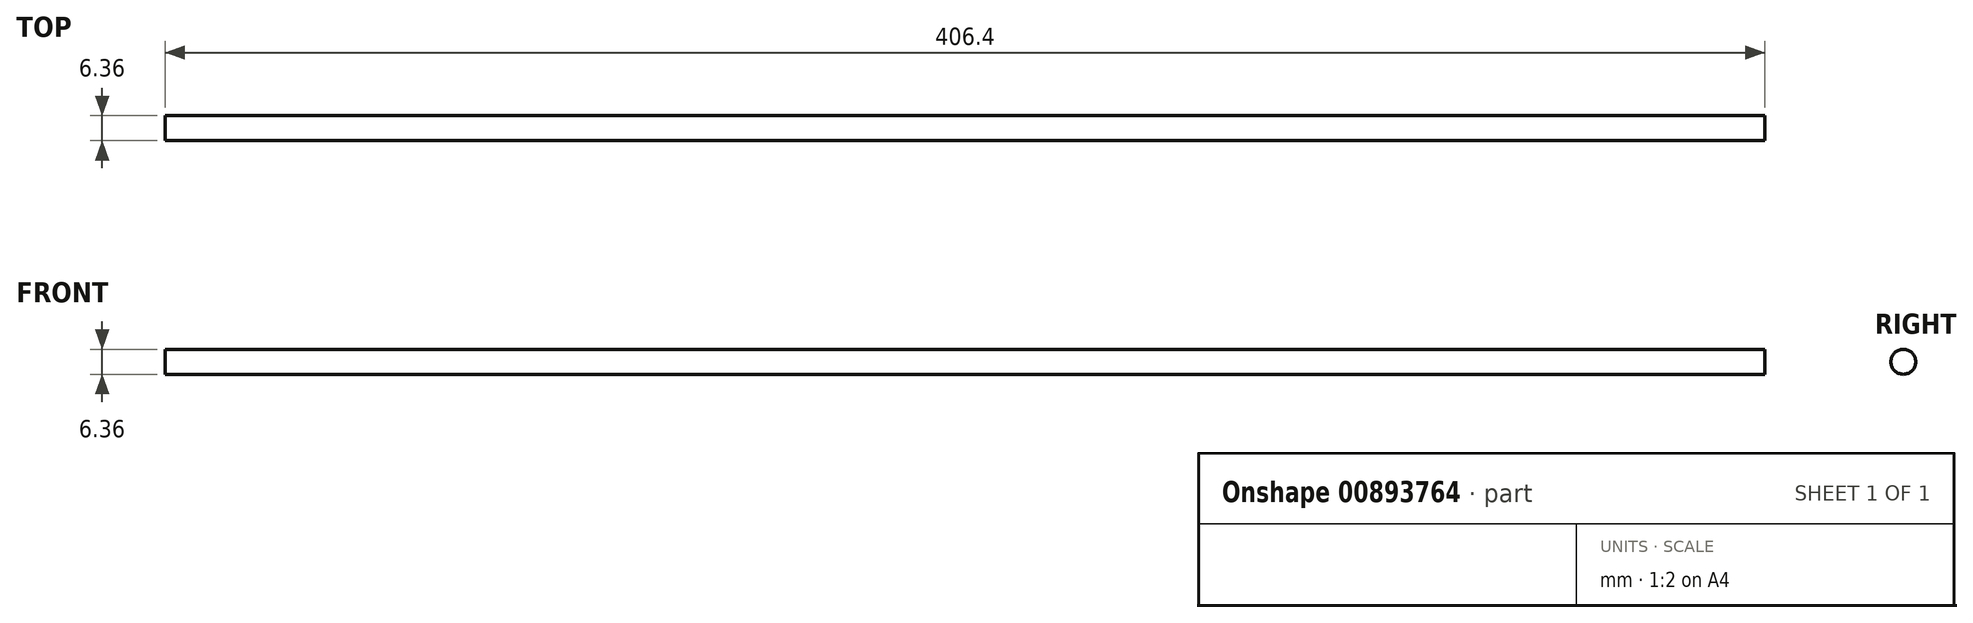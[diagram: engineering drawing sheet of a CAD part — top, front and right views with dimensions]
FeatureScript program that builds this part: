
annotation { "Feature Type Name" : "Feature", "Feature Type Description" : "" }
export const myFeature = defineFeature(function(context is Context, id is Id, definition is map)
    precondition{}
    {
        {
            var Q0;
            Q0=qCreatedBy(makeId("Right.planeOp"),FACE);
            var sketch = newSketch(context, id + "F0", { "sketchPlane" : qUnion([Q0])});
            skCircle(sketch, "E0", {"center": v(0, 0) * mm, "radius": 3.18 * mm});
            skSolve(sketch);
        }
        {
            var Q0;
            Q0 = qSketchRegion(id + "F0", true);
            extrude(context, id + "F1", {"entities" : qUnion([Q0]), "depth" : 203.2 * mm, "offsetDistance" : 25.4 * mm, "hasSecondDirection" : true, "secondDirectionOppositeDirection" : true, "secondDirectionDepth" : 203.2 * mm});
        }
    });
